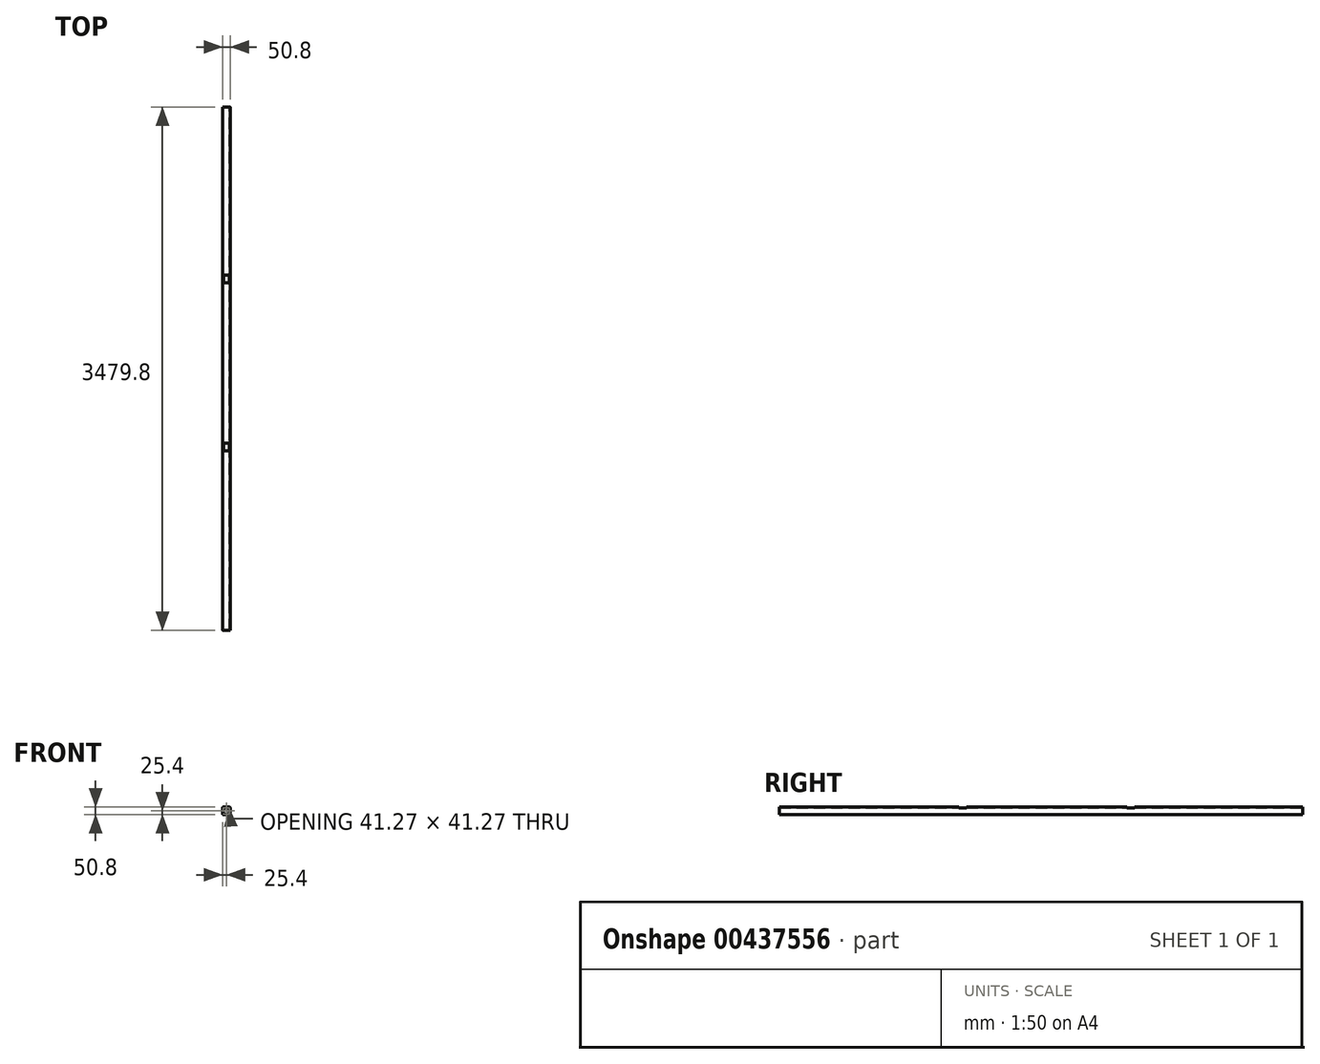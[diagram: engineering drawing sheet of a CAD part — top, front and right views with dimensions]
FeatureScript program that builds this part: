
annotation { "Feature Type Name" : "Feature", "Feature Type Description" : "" }
export const myFeature = defineFeature(function(context is Context, id is Id, definition is map)
    precondition{}
    {
        {
            var Q0;
            Q0=qCreatedBy(makeId("Front.planeOp"),FACE);
            var sketch = newSketch(context, id + "F0", { "sketchPlane" : qUnion([Q0])});
            skLineSegment(sketch, "E0.bottom", {"start": v(0, 0) * mm, "end": v(50.8, 0) * mm});
            skLineSegment(sketch, "E0.top", {"start": v(0, 50.8) * mm, "end": v(50.8, 50.8) * mm});
            skLineSegment(sketch, "E0.left", {"start": v(0, 0) * mm, "end": v(0, 50.8) * mm});
            skLineSegment(sketch, "E0.right", {"start": v(50.8, 0) * mm, "end": v(50.8, 50.8) * mm});
            skLineSegment(sketch, "E1.bottom", {"start": v(46.04, 4.76) * mm, "end": v(4.76, 4.76) * mm});
            skLineSegment(sketch, "E1.top", {"start": v(46.04, 46.04) * mm, "end": v(4.76, 46.04) * mm});
            skLineSegment(sketch, "E1.left", {"start": v(46.04, 4.76) * mm, "end": v(46.04, 46.04) * mm});
            skLineSegment(sketch, "E1.right", {"start": v(4.76, 4.76) * mm, "end": v(4.76, 46.04) * mm});
            skPoint(sketch, "E1.middle", {"position": v(25.4, 25.4) * mm});
            skPoint(sketch, "E1.middle.positionSnap0", {"position": v(50.8, 25.4) * mm});
            skPoint(sketch, "E1.middle.positionSnap1", {"position": v(25.4, 50.8) * mm});
            skPoint(sketch, "E1.centerSnap0", {"position": v(50.8, 25.4) * mm});
            skPoint(sketch, "E1.centerSnap1", {"position": v(25.4, 50.8) * mm});
            skSolve(sketch);
        }
        {
            var Q0;
            Q0 = qSketchRegion(id + "F0", true);
            extrude(context, id + "F1", {"entities" : qUnion([Q0]), "endBound" : BoundingType.SYMMETRIC, "depth" : 3479.8 * mm});
        }
        {
            var Q0;
            Q0=makeQuery(id+"F1.opExtrude","SWEPT_EDGE",EDGE,{"disambiguationData":[OSD([sQuery(id+"F0.wireOp",EDGE,"E0.top"),sQuery(id+"F0.wireOp",EDGE,"E0.right")])]});
            var Q1;
            Q1=makeQuery(id+"F1.opExtrude","SWEPT_EDGE",EDGE,{"disambiguationData":[OSD([sQuery(id+"F0.wireOp",EDGE,"E0.top"),sQuery(id+"F0.wireOp",EDGE,"E0.left")])]});
            var Q2;
            Q2=makeQuery(id+"F1.opExtrude","SWEPT_EDGE",EDGE,{"disambiguationData":[OSD([sQuery(id+"F0.wireOp",EDGE,"E1.top"),sQuery(id+"F0.wireOp",EDGE,"E1.right")])]});
            var Q3;
            Q3=makeQuery(id+"F1.opExtrude","SWEPT_EDGE",EDGE,{"disambiguationData":[OSD([sQuery(id+"F0.wireOp",EDGE,"E1.bottom"),sQuery(id+"F0.wireOp",EDGE,"E1.left")])]});
            var Q4;
            Q4=makeQuery(id+"F1.opExtrude","SWEPT_EDGE",EDGE,{"disambiguationData":[OSD([sQuery(id+"F0.wireOp",EDGE,"E1.bottom"),sQuery(id+"F0.wireOp",EDGE,"E1.right")])]});
            var Q5;
            Q5=makeQuery(id+"F1.opExtrude","SWEPT_EDGE",EDGE,{"disambiguationData":[OSD([sQuery(id+"F0.wireOp",EDGE,"E1.top"),sQuery(id+"F0.wireOp",EDGE,"E1.left")])]});
            var Q6;
            Q6=makeQuery(id+"F1.opExtrude","SWEPT_EDGE",EDGE,{"disambiguationData":[OSD([sQuery(id+"F0.wireOp",EDGE,"E0.bottom"),sQuery(id+"F0.wireOp",EDGE,"E0.left")])]});
            var Q7;
            Q7=makeQuery(id+"F1.opExtrude","SWEPT_EDGE",EDGE,{"disambiguationData":[OSD([sQuery(id+"F0.wireOp",EDGE,"E0.bottom"),sQuery(id+"F0.wireOp",EDGE,"E0.right")])]});
            fillet(context, id + "F2", {"entities" : qUnion([Q0, Q1, Q2, Q3, Q4, Q5, Q6, Q7]), "radius" : 5.08 * mm, "tangentPropagation" : true, "allowEdgeOverflow" : false});
        }
        {
            var Q0;
            Q0=makeQuery(id+"F1.opExtrude","SWEPT_FACE",FACE,{"disambiguationData":[OSD([sQuery(id+"F0.wireOp",EDGE,"E0.top")])]});
            var sketch = newSketch(context, id + "F3", { "sketchPlane" : qUnion([Q0])});
            skLineSegment(sketch, "E2.bottom", {"start": v(0, -546.1) * mm, "end": v(50.8, -546.1) * mm});
            skLineSegment(sketch, "E2.top", {"start": v(0, -495.3) * mm, "end": v(50.8, -495.3) * mm});
            skLineSegment(sketch, "E2.left", {"start": v(0, -546.1) * mm, "end": v(0, -495.3) * mm});
            skLineSegment(sketch, "E2.right", {"start": v(50.8, -546.1) * mm, "end": v(50.8, -495.3) * mm});
            skLineSegment(sketch, "E3.bottom", {"start": v(0, 571.5) * mm, "end": v(50.8, 571.5) * mm});
            skLineSegment(sketch, "E3.top", {"start": v(0, 622.3) * mm, "end": v(50.8, 622.3) * mm});
            skLineSegment(sketch, "E3.left", {"start": v(0, 571.5) * mm, "end": v(0, 622.3) * mm});
            skLineSegment(sketch, "E3.right", {"start": v(50.8, 571.5) * mm, "end": v(50.8, 622.3) * mm});
            skSolve(sketch);
        }
        {
            var Q0;
            Q0 = qSketchRegion(id + "F3", true);
            extrude(context, id + "F4", {"entities" : qUnion([Q0]), "operationType" : NewBodyOperationType.REMOVE, "oppositeDirection" : true, "depth" : 6.35 * mm});
        }
    });
